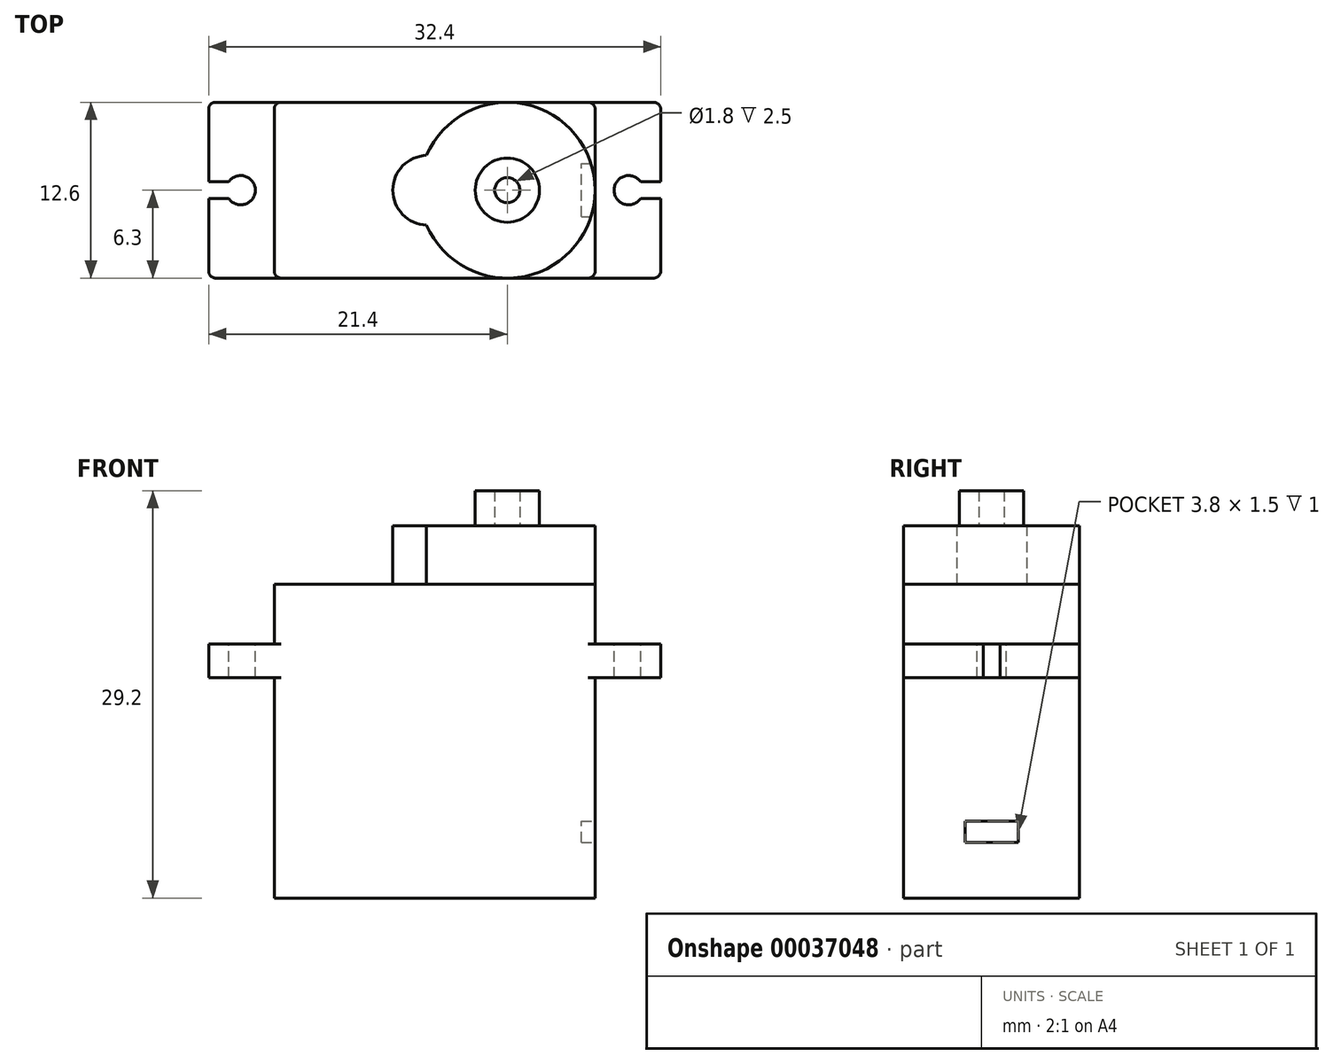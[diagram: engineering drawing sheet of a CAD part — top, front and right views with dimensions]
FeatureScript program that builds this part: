
annotation { "Feature Type Name" : "Feature", "Feature Type Description" : "" }
export const myFeature = defineFeature(function(context is Context, id is Id, definition is map)
    precondition{}
    {
        {
            var Q0;
            Q0=qCreatedBy(makeId("Front.planeOp"),FACE);
            var sketch = newSketch(context, id + "F0", { "sketchPlane" : qUnion([Q0])});
            skLineSegment(sketch, "E0.bottom", {"start": v(0, 0) * mm, "end": v(23, 0) * mm});
            skLineSegment(sketch, "E0.top", {"start": v(0, 22.5) * mm, "end": v(23, 22.5) * mm});
            skLineSegment(sketch, "E0.left", {"start": v(0, 0) * mm, "end": v(0, 22.5) * mm});
            skLineSegment(sketch, "E0.right", {"start": v(23, 0) * mm, "end": v(23, 22.5) * mm});
            skLineSegment(sketch, "E1.bottom", {"start": v(0, 15.8) * mm, "end": v(-4.7, 15.8) * mm});
            skLineSegment(sketch, "E1.top", {"start": v(0, 18.2) * mm, "end": v(-4.7, 18.2) * mm});
            skLineSegment(sketch, "E1.left", {"start": v(0, 15.8) * mm, "end": v(0, 18.2) * mm});
            skLineSegment(sketch, "E1.right", {"start": v(-4.7, 15.8) * mm, "end": v(-4.7, 18.2) * mm});
            skLineSegment(sketch, "E2", {"start": v(11.5, 0) * mm, "end": v(11.5, 38.16) * mm, "construction": true});
            skLineSegment(sketch, "E3.0.MirrorCS", {"start": v(27.7, 15.8) * mm, "end": v(27.7, 18.2) * mm});
            skLineSegment(sketch, "E4.0.MirrorCS", {"start": v(23, 18.2) * mm, "end": v(27.7, 18.2) * mm});
            skLineSegment(sketch, "E5.0.MirrorCS", {"start": v(23, 15.8) * mm, "end": v(27.7, 15.8) * mm});
            skSolve(sketch);
        }
        {
            var Q0;
            Q0=qSketchRegion(id+"F0",true);
            extrude(context, id + "F1", {"entities" : qUnion([Q0]), "depth" : 12.6 * mm});
        }
        {
            var Q0;
            Q0=makeQuery(id+"F1.opExtrude","SWEPT_FACE",FACE,{"disambiguationData":[OSD([sQuery(id+"F0.wireOp",EDGE,"E0.top")])]});
            var sketch = newSketch(context, id + "F2", { "sketchPlane" : qUnion([Q0])});
            skLineSegment(sketch, "E6", {"start": v(23, -6.3) * mm, "end": v(0, -6.3) * mm, "construction": true});
            skArc(sketch, "E7", {"start": v(10.92, -8.8) * mm, "mid": v(23, -6.3) * mm, "end": v(10.92, -3.8) * mm});
            skArc(sketch, "E8", {"start": v(10.92, -3.8) * mm, "mid": v(8.5, -6.3) * mm, "end": v(10.92, -8.8) * mm});
            skSolve(sketch);
        }
        {
            var Q0;
            Q0=qSketchRegion(id+"F2",true);
            extrude(context, id + "F3", {"entities" : qUnion([Q0]), "operationType" : NewBodyOperationType.ADD, "depth" : (26.7 - 22.5) * mm});
        }
        {
            var Q0;
            Q0=makeQuery(id+"F3.opExtrude","CAP_FACE",FACE,{"disambiguationData":[OSD([sQuery(id+"F2.wireOp",EDGE,"E7"),sQuery(id+"F2.wireOp",EDGE,"E8")])],"isStart":false});
            var sketch = newSketch(context, id + "F4", { "sketchPlane" : qUnion([Q0])});
            skCircle(sketch, "E9", {"center": v(16.7, -6.3) * mm, "radius": 0.9 * mm});
            skCircle(sketch, "E10", {"center": v(16.7, -6.3) * mm, "radius": 2.3 * mm});
            skSolve(sketch);
        }
        {
            var Q0;
            Q0=qSketchRegion(id+"F4",true);
            extrude(context, id + "F5", {"entities" : qUnion([Q0]), "operationType" : NewBodyOperationType.ADD, "depth" : (29.2 - 26.7) * mm});
        }
        {
            var Q0;
            Q0=makeQuery(id+"F1.opExtrude","SWEPT_FACE",FACE,{"disambiguationData":[OSD([sQuery(id+"F0.wireOp",EDGE,"E1.top")])]});
            var sketch = newSketch(context, id + "F6", { "sketchPlane" : qUnion([Q0])});
            skLineSegment(sketch, "E11", {"start": v(-4.7, -6.3) * mm, "end": v(30.63, -6.3) * mm, "construction": true});
            skLineSegment(sketch, "E12.0", {"start": v(0, -12.6) * mm, "end": v(23, -12.6) * mm, "construction": true});
            skLineSegment(sketch, "E13.0", {"start": v(0, 0) * mm, "end": v(23, 0) * mm, "construction": true});
            skLineSegment(sketch, "E14", {"start": v(11.5, 0) * mm, "end": v(11.5, -12.6) * mm, "construction": true});
            skArc(sketch, "E15", {"start": v(-3.26, -6.9) * mm, "mid": v(-1.35, -6.3) * mm, "end": v(-3.26, -5.7) * mm});
            skArc(sketch, "E16.0.MirrorC", {"start": v(26.26, -6.9) * mm, "mid": v(24.35, -6.3) * mm, "end": v(26.26, -5.7) * mm});
            skLineSegment(sketch, "E17.bottom", {"start": v(-5.39, -6.9) * mm, "end": v(-3.26, -6.9) * mm});
            skLineSegment(sketch, "E17.top", {"start": v(-5.39, -5.7) * mm, "end": v(-3.26, -5.7) * mm});
            skLineSegment(sketch, "E17.left", {"start": v(-5.39, -6.9) * mm, "end": v(-5.39, -5.7) * mm});
            skLineSegment(sketch, "E18.0.MirrorCS", {"start": v(28.39, -6.9) * mm, "end": v(26.26, -6.9) * mm});
            skLineSegment(sketch, "E18.1.MirrorCS", {"start": v(28.39, -5.7) * mm, "end": v(26.26, -5.7) * mm});
            skLineSegment(sketch, "E18.3.MirrorCS", {"start": v(28.39, -6.9) * mm, "end": v(28.39, -5.7) * mm});
            skSolve(sketch);
        }
        {
            var Q0;
            Q0=qSketchRegion(id+"F6",true);
            extrude(context, id + "F7", {"entities" : qUnion([Q0]), "operationType" : NewBodyOperationType.REMOVE, "oppositeDirection" : true, "depth" : 25 * mm});
        }
        {
            var Q0;
            {var subQ0=sQuery(id+"F0.wireOp",EDGE,"E0.left");Q0=makeQuery(id+"F1.opExtrude","CAP_EDGE",EDGE,{"disambiguationData":[OSD([subQ0]),TDD([makeQuery(id+"F0.imprint","IMPRINT",EDGE,{"disambiguationData":[TD([[makeQuery(id+"F0.imprint","INTERSECT",VERTEX,{"derivedFrom":[sQuery(id+"F0.wireOp",EDGE,"E0.top"),subQ0]}),1.0]])],"derivedFrom":subQ0})])],"isStart":false});}
            var Q1;
            {var subQ0=sQuery(id+"F0.wireOp",EDGE,"E0.left");Q1=makeQuery(id+"F1.opExtrude","CAP_EDGE",EDGE,{"disambiguationData":[OSD([subQ0]),TDD([makeQuery(id+"F0.imprint","IMPRINT",EDGE,{"disambiguationData":[TD([[makeQuery(id+"F0.imprint","INTERSECT",VERTEX,{"derivedFrom":[sQuery(id+"F0.wireOp",EDGE,"E0.bottom"),subQ0]}),-1.0]])],"derivedFrom":subQ0})])],"isStart":false});}
            var Q2;
            {var subQ0=sQuery(id+"F0.wireOp",EDGE,"E0.left");Q2=makeQuery(id+"F1.opExtrude","CAP_EDGE",EDGE,{"disambiguationData":[OSD([subQ0]),TDD([makeQuery(id+"F0.imprint","IMPRINT",EDGE,{"disambiguationData":[TD([[makeQuery(id+"F0.imprint","INTERSECT",VERTEX,{"derivedFrom":[sQuery(id+"F0.wireOp",EDGE,"E0.top"),subQ0]}),1.0]])],"derivedFrom":subQ0})])],"isStart":true});}
            var Q3;
            {var subQ0=sQuery(id+"F0.wireOp",EDGE,"E0.left");Q3=makeQuery(id+"F1.opExtrude","CAP_EDGE",EDGE,{"disambiguationData":[OSD([subQ0]),TDD([makeQuery(id+"F0.imprint","IMPRINT",EDGE,{"disambiguationData":[TD([[makeQuery(id+"F0.imprint","INTERSECT",VERTEX,{"derivedFrom":[sQuery(id+"F0.wireOp",EDGE,"E0.bottom"),subQ0]}),-1.0]])],"derivedFrom":subQ0})])],"isStart":true});}
            var Q4;
            Q4=makeQuery(id+"F1.opExtrude","CAP_EDGE",EDGE,{"disambiguationData":[OSD([sQuery(id+"F0.wireOp",EDGE,"E1.right")])],"isStart":false});
            var Q5;
            Q5=makeQuery(id+"F1.opExtrude","CAP_EDGE",EDGE,{"disambiguationData":[OSD([sQuery(id+"F0.wireOp",EDGE,"E1.right")])],"isStart":true});
            var Q6;
            Q6=makeQuery(id+"F1.opExtrude","CAP_EDGE",EDGE,{"disambiguationData":[OSD([sQuery(id+"F0.wireOp",EDGE,"E3.0.MirrorCS")])],"isStart":false});
            var Q7;
            {var subQ0=sQuery(id+"F0.wireOp",EDGE,"E0.right");Q7=makeQuery(id+"F1.opExtrude","CAP_EDGE",EDGE,{"disambiguationData":[OSD([subQ0]),TDD([makeQuery(id+"F0.imprint","IMPRINT",EDGE,{"disambiguationData":[TD([[makeQuery(id+"F0.imprint","INTERSECT",VERTEX,{"derivedFrom":[sQuery(id+"F0.wireOp",EDGE,"E0.top"),subQ0]}),1.0]])],"derivedFrom":subQ0})])],"isStart":false});}
            var Q8;
            {var subQ0=sQuery(id+"F0.wireOp",EDGE,"E0.right");Q8=makeQuery(id+"F1.opExtrude","CAP_EDGE",EDGE,{"disambiguationData":[OSD([subQ0]),TDD([makeQuery(id+"F0.imprint","IMPRINT",EDGE,{"disambiguationData":[TD([[makeQuery(id+"F0.imprint","INTERSECT",VERTEX,{"derivedFrom":[sQuery(id+"F0.wireOp",EDGE,"E0.bottom"),subQ0]}),-1.0]])],"derivedFrom":subQ0})])],"isStart":false});}
            var Q9;
            Q9=makeQuery(id+"F1.opExtrude","CAP_EDGE",EDGE,{"disambiguationData":[OSD([sQuery(id+"F0.wireOp",EDGE,"E3.0.MirrorCS")])],"isStart":true});
            var Q10;
            {var subQ0=sQuery(id+"F0.wireOp",EDGE,"E0.right");Q10=makeQuery(id+"F1.opExtrude","CAP_EDGE",EDGE,{"disambiguationData":[OSD([subQ0]),TDD([makeQuery(id+"F0.imprint","IMPRINT",EDGE,{"disambiguationData":[TD([[makeQuery(id+"F0.imprint","INTERSECT",VERTEX,{"derivedFrom":[sQuery(id+"F0.wireOp",EDGE,"E0.top"),subQ0]}),1.0]])],"derivedFrom":subQ0})])],"isStart":true});}
            var Q11;
            {var subQ0=sQuery(id+"F0.wireOp",EDGE,"E0.right");Q11=makeQuery(id+"F1.opExtrude","CAP_EDGE",EDGE,{"disambiguationData":[OSD([subQ0]),TDD([makeQuery(id+"F0.imprint","IMPRINT",EDGE,{"disambiguationData":[TD([[makeQuery(id+"F0.imprint","INTERSECT",VERTEX,{"derivedFrom":[sQuery(id+"F0.wireOp",EDGE,"E0.bottom"),subQ0]}),-1.0]])],"derivedFrom":subQ0})])],"isStart":true});}
            fillet(context, id + "F8", {"entities" : qUnion([Q0, Q1, Q2, Q3, Q4, Q5, Q6, Q7, Q8, Q9, Q10, Q11]), "radius" : 0.5 * mm, "tangentPropagation" : true, "allowEdgeOverflow" : false});
        }
        {
            var Q0;
            {var subQ0=sQuery(id+"F0.wireOp",EDGE,"E0.right");Q0=makeQuery(id+"F1.opExtrude","SWEPT_FACE",FACE,{"disambiguationData":[OSD([subQ0]),TDD([makeQuery(id+"F0.imprint","IMPRINT",EDGE,{"disambiguationData":[TD([[makeQuery(id+"F0.imprint","INTERSECT",VERTEX,{"derivedFrom":[sQuery(id+"F0.wireOp",EDGE,"E0.bottom"),subQ0]}),-1.0]])],"derivedFrom":subQ0})])]});}
            var sketch = newSketch(context, id + "F9", { "sketchPlane" : qUnion([Q0])});
            skLineSegment(sketch, "E19.bottom", {"start": v(-8.2, 4) * mm, "end": v(-4.4, 4) * mm});
            skLineSegment(sketch, "E19.top", {"start": v(-8.2, 5.5) * mm, "end": v(-4.4, 5.5) * mm});
            skLineSegment(sketch, "E19.left", {"start": v(-8.2, 4) * mm, "end": v(-8.2, 5.5) * mm});
            skLineSegment(sketch, "E19.right", {"start": v(-4.4, 4) * mm, "end": v(-4.4, 5.5) * mm});
            skLineSegment(sketch, "E20", {"start": v(-6.3, 0) * mm, "end": v(-6.3, 11.49) * mm, "construction": true});
            skSolve(sketch);
        }
        {
            var Q0;
            Q0=qSketchRegion(id+"F9",true);
            extrude(context, id + "F10", {"entities" : qUnion([Q0]), "operationType" : NewBodyOperationType.REMOVE, "oppositeDirection" : true, "depth" : 1 * mm});
        }
    });
